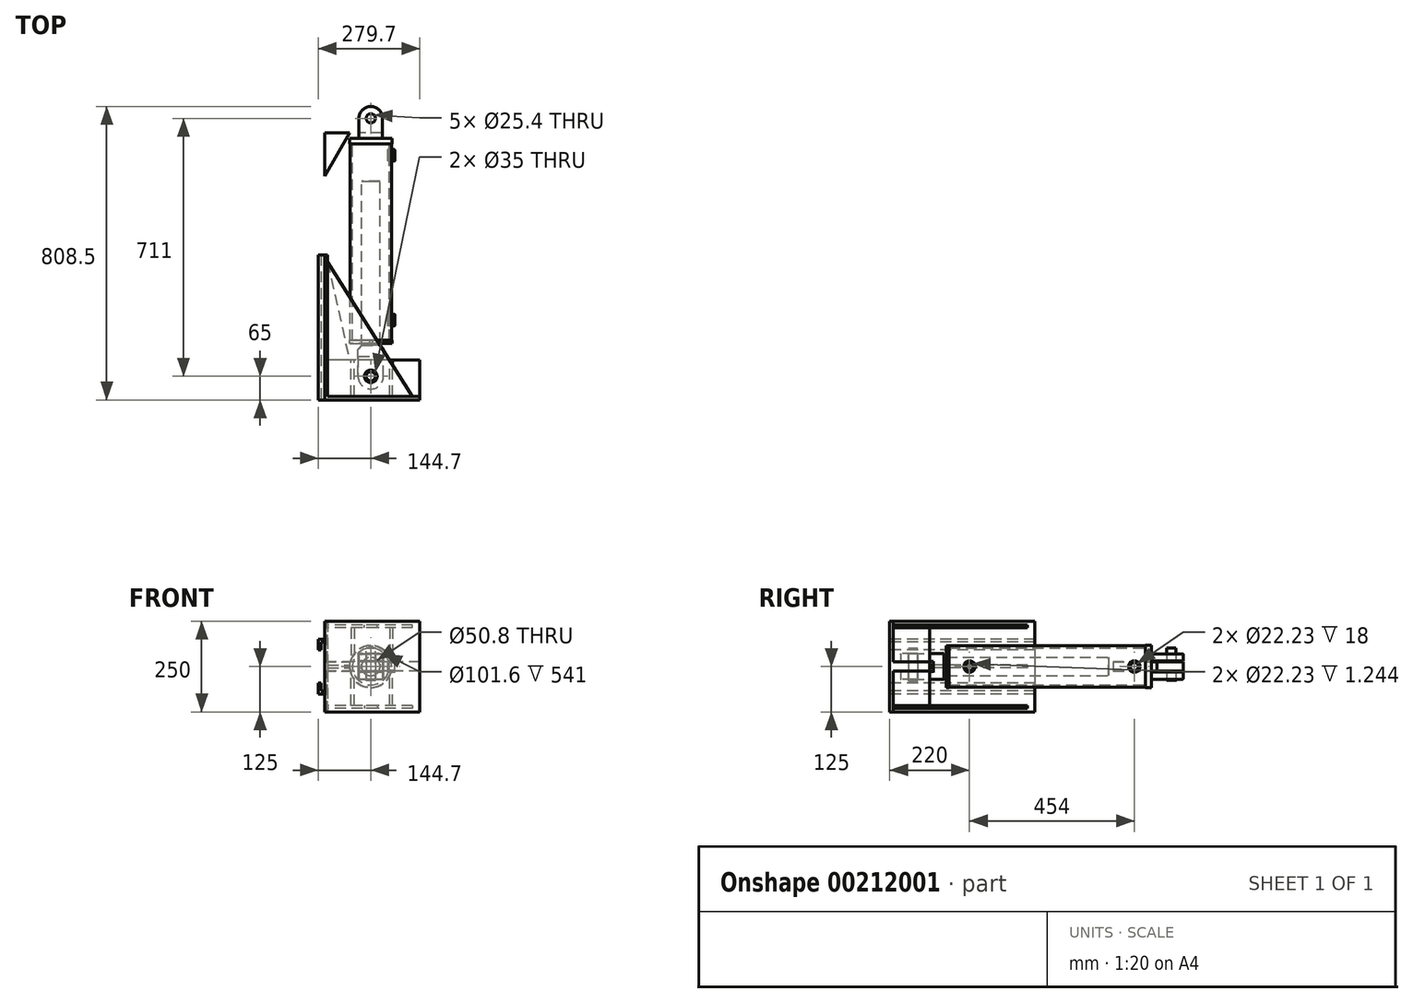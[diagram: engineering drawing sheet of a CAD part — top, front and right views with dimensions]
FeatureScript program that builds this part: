
annotation { "Feature Type Name" : "Feature", "Feature Type Description" : "" }
export const myFeature = defineFeature(function(context is Context, id is Id, definition is map)
    precondition{}
    {
        {
            assignVariable(context, id + "F0", {"name" : "Stroke", "anyValue" : 400});
        }
        {
            var Q0;
            Q0=qCreatedBy(makeId("Front.planeOp"),FACE);
            var sketch = newSketch(context, id + "F1", { "sketchPlane" : qUnion([Q0])});
            skCircle(sketch, "E0", {"center": v(0, 0) * mm, "radius": 50.8 * mm});
            skCircle(sketch, "E1", {"center": v(0, 0) * mm, "radius": 57.15 * mm});
            skSolve(sketch);
        }
        {
            var Q0;
            Q0=makeQuery(id+"F1.imprint","IMPRINT",FACE,{"disambiguationData":[TD([[makeQuery(id+"F1.imprint","IMPRINT",EDGE,{"derivedFrom":sQuery(id+"F1.wireOp",EDGE,"E0")}),-1.0]])]});
            extrude(context, id + "F2", {"entities" : qUnion([Q0]), "depth" : (getVariable(context, 'Stroke') + 141) * mm});
        }
        {
            var Q0;
            Q0=makeQuery(id+"F2.opExtrude","CAP_FACE",FACE,{"disambiguationData":[OSD([sQuery(id+"F1.wireOp",EDGE,"E0"),sQuery(id+"F1.wireOp",EDGE,"E1")])],"isStart":true});
            var sketch = newSketch(context, id + "F3", { "sketchPlane" : qUnion([Q0])});
            skCircle(sketch, "E2", {"center": v(0, 0) * mm, "radius": 58.15 * mm});
            skSolve(sketch);
        }
        {
            var Q0;
            Q0=makeQuery(id+"F3.imprint","IMPRINT",FACE,{"disambiguationData":[TD([[makeQuery(id+"F3.imprint","IMPRINT",EDGE,{"derivedFrom":makeQuery(id+"F2.opExtrude","CAP_EDGE",EDGE,{"disambiguationData":[OSD([sQuery(id+"F1.wireOp",EDGE,"E0")])],"isStart":true})}),1.0]])]});
            var Q1;
            Q1=makeQuery(id+"F3.imprint","IMPRINT",FACE,{"disambiguationData":[TD([[makeQuery(id+"F3.imprint","IMPRINT",EDGE,{"derivedFrom":sQuery(id+"F3.wireOp",EDGE,"E2")}),1.0]])]});
            var Q2;
            Q2=makeQuery(id+"F3.imprint","IMPRINT",FACE,{"disambiguationData":[TD([[makeQuery(id+"F3.imprint","IMPRINT",EDGE,{"derivedFrom":makeQuery(id+"F2.opExtrude","CAP_EDGE",EDGE,{"disambiguationData":[OSD([sQuery(id+"F1.wireOp",EDGE,"E0")])],"isStart":true})}),-1.0]])]});
            extrude(context, id + "F4", {"entities" : qUnion([Q0, Q1, Q2]), "depth" : 16 * mm});
        }
        {
            var Q0;
            Q0=makeQuery(id+"F2.opExtrude","CAP_FACE",FACE,{"disambiguationData":[OSD([sQuery(id+"F1.wireOp",EDGE,"E0"),sQuery(id+"F1.wireOp",EDGE,"E1")])],"isStart":false});
            var sketch = newSketch(context, id + "F5", { "sketchPlane" : qUnion([Q0])});
            skCircle(sketch, "E3", {"center": v(0, 0) * mm, "radius": 58.15 * mm});
            skCircle(sketch, "E4", {"center": v(0, 0) * mm, "radius": 25.4 * mm});
            skSolve(sketch);
        }
        {
            var Q0;
            Q0=makeQuery(id+"F5.imprint","IMPRINT",FACE,{"disambiguationData":[TD([[makeQuery(id+"F5.imprint","IMPRINT",EDGE,{"derivedFrom":makeQuery(id+"F2.opExtrude","CAP_EDGE",EDGE,{"disambiguationData":[OSD([sQuery(id+"F1.wireOp",EDGE,"E0")])],"isStart":false})}),-1.0]])]});
            var Q1;
            Q1=makeQuery(id+"F5.imprint","IMPRINT",FACE,{"disambiguationData":[TD([[makeQuery(id+"F5.imprint","IMPRINT",EDGE,{"derivedFrom":sQuery(id+"F5.wireOp",EDGE,"E4")}),-1.0]])]});
            var Q2;
            Q2=makeQuery(id+"F5.imprint","IMPRINT",FACE,{"disambiguationData":[TD([[makeQuery(id+"F5.imprint","IMPRINT",EDGE,{"derivedFrom":sQuery(id+"F5.wireOp",EDGE,"E3")}),1.0]])]});
            extrude(context, id + "F6", {"entities" : qUnion([Q0, Q1, Q2]), "depth" : 8 * mm});
        }
        {
            var Q0;
            Q0=makeQuery(id+"F6.opExtrude","CAP_FACE",FACE,{"disambiguationData":[OSD([sQuery(id+"F5.wireOp",EDGE,"E3"),sQuery(id+"F5.wireOp",EDGE,"E4")])],"isStart":false});
            var sketch = newSketch(context, id + "F7", { "sketchPlane" : qUnion([Q0])});
            skLineSegment(sketch, "E5", {"start": v(-3.5, 58.04) * mm, "end": v(-3.5, 54.04) * mm});
            skLineSegment(sketch, "E6", {"start": v(-3.5, 54.04) * mm, "end": v(3.5, 54.04) * mm});
            skLineSegment(sketch, "E7", {"start": v(3.5, 54.04) * mm, "end": v(3.5, 58.04) * mm});
            skPoint(sketch, "E8", {"position": v(0, 54.04) * mm});
            skCircle(sketch, "E9.0", {"center": v(0, 0) * mm, "radius": 58.15 * mm});
            skArc(sketch, "E10", {"start": v(-3.5, 58.04) * mm, "mid": v(0, 58.15) * mm, "end": v(3.5, 58.04) * mm});
            skSolve(sketch);
        }
        {
            var Q0;
            {var subQ0=sQuery(id+"F7.wireOp",EDGE,"E5");Q0=makeQuery(id+"F7.imprint","IMPRINT",FACE,{"disambiguationData":[TD([[makeQuery(id+"F7.imprint","IMPRINT",EDGE,{"derivedFrom":subQ0}),1.0]])]});}
            extrude(context, id + "F8", {"entities" : qUnion([Q0]), "operationType" : NewBodyOperationType.REMOVE, "endBound" : BoundingType.UP_TO_NEXT, "oppositeDirection" : true, "depth" : 25 * mm});
        }
        {
            var Q0;
            Q0=qCreatedBy(makeId("Top.planeOp"),FACE);
            var sketch = newSketch(context, id + "F9", { "sketchPlane" : qUnion([Q0])});
            skCircle(sketch, "E11", {"center": v(0, 71) * mm, "radius": 12.7 * mm});
            skCircle(sketch, "E12", {"center": v(0, 71) * mm, "radius": 32.5 * mm});
            skLineSegment(sketch, "E13.0", {"start": v(-58.15, 16) * mm, "end": v(58.15, 16) * mm});
            skLineSegment(sketch, "E14", {"start": v(-32.5, 16) * mm, "end": v(-32.5, 71) * mm});
            skLineSegment(sketch, "E15", {"start": v(32.5, 16) * mm, "end": v(32.5, 71) * mm});
            skSolve(sketch);
        }
        {
            var Q0;
            {var subQ0=sQuery(id+"F9.wireOp",EDGE,"E14");Q0=makeQuery(id+"F9.imprint","IMPRINT",FACE,{"disambiguationData":[TD([[makeQuery(id+"F9.imprint","IMPRINT",EDGE,{"derivedFrom":subQ0}),-1.0]])]});}
            var Q1;
            Q1=makeQuery(id+"F9.imprint","IMPRINT",FACE,{"disambiguationData":[TD([[makeQuery(id+"F9.imprint","IMPRINT",EDGE,{"derivedFrom":sQuery(id+"F9.wireOp",EDGE,"E11")}),-1.0]])]});
            extrude(context, id + "F10", {"entities" : qUnion([Q0, Q1]), "operationType" : NewBodyOperationType.ADD, "endBound" : BoundingType.SYMMETRIC, "depth" : 70 * mm});
        }
        {
            var Q0;
            {var subQ0=sQuery(id+"F9.wireOp",EDGE,"E14");Q0=makeQuery(id+"F9.imprint","IMPRINT",FACE,{"disambiguationData":[TD([[makeQuery(id+"F9.imprint","IMPRINT",EDGE,{"derivedFrom":subQ0}),-1.0]])]});}
            var Q1;
            Q1=makeQuery(id+"F9.imprint","IMPRINT",FACE,{"disambiguationData":[TD([[makeQuery(id+"F9.imprint","IMPRINT",EDGE,{"derivedFrom":sQuery(id+"F9.wireOp",EDGE,"E11")}),-1.0]])]});
            extrude(context, id + "F11", {"entities" : qUnion([Q0, Q1]), "operationType" : NewBodyOperationType.REMOVE, "endBound" : BoundingType.SYMMETRIC, "depth" : 30 * mm});
        }
        {
            var Q0;
            Q0=makeQuery(id+"F10.opExtrude","CAP_EDGE",EDGE,{"disambiguationData":[OSD([sQuery(id+"F9.wireOp",EDGE,"E13.0")])],"isStart":false});
            var Q1;
            {var subQ0=sQuery(id+"F9.wireOp",EDGE,"E14");var subQ1=sQuery(id+"F9.wireOp",EDGE,"E15");var subQ2=sQuery(id+"F9.wireOp",EDGE,"E13.0");var subQ3=sQuery(id+"F9.wireOp",EDGE,"E12");var subQ4=sQuery(id+"F9.wireOp",EDGE,"E11");Q1=makeQuery(id+"F11.boolean.opBoolean","SPLIT",EDGE,{"disambiguationData":[TD([makeQuery(id+"F10.opExtrude","CAP_FACE",FACE,{"disambiguationData":[OSD([subQ4,subQ3,subQ2,subQ0,subQ1])],"isStart":false})])],"derivedFrom":makeQuery(id+"F10.opExtrude","SWEPT_EDGE",EDGE,{"disambiguationData":[OSD([subQ2,subQ0])]})});}
            var Q2;
            Q2=makeQuery(id+"F11.boolean.opBoolean","COPY",EDGE,{"derivedFrom":makeQuery(id+"F11.opExtrude","CAP_EDGE",EDGE,{"disambiguationData":[OSD([sQuery(id+"F9.wireOp",EDGE,"E13.0")])],"isStart":false})});
            var Q3;
            Q3=makeQuery(id+"F10.opExtrude","CAP_EDGE",EDGE,{"disambiguationData":[OSD([sQuery(id+"F9.wireOp",EDGE,"E13.0")])],"isStart":true});
            var Q4;
            {var subQ0=sQuery(id+"F9.wireOp",EDGE,"E14");var subQ1=sQuery(id+"F9.wireOp",EDGE,"E15");var subQ2=sQuery(id+"F9.wireOp",EDGE,"E13.0");var subQ3=sQuery(id+"F9.wireOp",EDGE,"E12");var subQ4=sQuery(id+"F9.wireOp",EDGE,"E11");Q4=makeQuery(id+"F11.boolean.opBoolean","SPLIT",EDGE,{"disambiguationData":[TD([makeQuery(id+"F10.opExtrude","CAP_FACE",FACE,{"disambiguationData":[OSD([subQ4,subQ3,subQ2,subQ0,subQ1])],"isStart":true})])],"derivedFrom":makeQuery(id+"F10.opExtrude","SWEPT_EDGE",EDGE,{"disambiguationData":[OSD([subQ2,subQ0])]})});}
            var Q5;
            Q5=makeQuery(id+"F11.boolean.opBoolean","COPY",EDGE,{"derivedFrom":makeQuery(id+"F11.opExtrude","CAP_EDGE",EDGE,{"disambiguationData":[OSD([sQuery(id+"F9.wireOp",EDGE,"E13.0")])],"isStart":true})});
            var Q6;
            {var subQ0=sQuery(id+"F9.wireOp",EDGE,"E15");var subQ1=sQuery(id+"F9.wireOp",EDGE,"E14");var subQ2=sQuery(id+"F9.wireOp",EDGE,"E13.0");var subQ3=sQuery(id+"F9.wireOp",EDGE,"E12");var subQ4=sQuery(id+"F9.wireOp",EDGE,"E11");Q6=makeQuery(id+"F11.boolean.opBoolean","SPLIT",EDGE,{"disambiguationData":[TD([makeQuery(id+"F10.opExtrude","CAP_FACE",FACE,{"disambiguationData":[OSD([subQ4,subQ3,subQ2,subQ1,subQ0])],"isStart":true})])],"derivedFrom":makeQuery(id+"F10.opExtrude","SWEPT_EDGE",EDGE,{"disambiguationData":[OSD([subQ2,subQ0])]})});}
            var Q7;
            {var subQ0=sQuery(id+"F9.wireOp",EDGE,"E15");var subQ1=sQuery(id+"F9.wireOp",EDGE,"E14");var subQ2=sQuery(id+"F9.wireOp",EDGE,"E13.0");var subQ3=sQuery(id+"F9.wireOp",EDGE,"E12");var subQ4=sQuery(id+"F9.wireOp",EDGE,"E11");Q7=makeQuery(id+"F11.boolean.opBoolean","SPLIT",EDGE,{"disambiguationData":[TD([makeQuery(id+"F10.opExtrude","CAP_FACE",FACE,{"disambiguationData":[OSD([subQ4,subQ3,subQ2,subQ1,subQ0])],"isStart":false})])],"derivedFrom":makeQuery(id+"F10.opExtrude","SWEPT_EDGE",EDGE,{"disambiguationData":[OSD([subQ2,subQ0])]})});}
            fillet(context, id + "F12", {"entities" : qUnion([Q0, Q1, Q2, Q3, Q4, Q5, Q6, Q7]), "radius" : 3 * mm, "tangentPropagation" : true, "allowEdgeOverflow" : false});
        }
        {
            var Q0;
            Q0=makeQuery(id+"F11.boolean.opBoolean","COPY",EDGE,{"derivedFrom":makeQuery(id+"F11.opExtrude","CAP_EDGE",EDGE,{"disambiguationData":[OSD([sQuery(id+"F9.wireOp",EDGE,"E12")])],"isStart":true})});
            var Q1;
            Q1=makeQuery(id+"F11.boolean.opBoolean","COPY",EDGE,{"derivedFrom":makeQuery(id+"F11.opExtrude","CAP_EDGE",EDGE,{"disambiguationData":[OSD([sQuery(id+"F9.wireOp",EDGE,"E12")])],"isStart":false})});
            var Q2;
            Q2=makeQuery(id+"F10.opExtrude","CAP_EDGE",EDGE,{"disambiguationData":[OSD([sQuery(id+"F9.wireOp",EDGE,"E12")])],"isStart":false});
            var Q3;
            Q3=makeQuery(id+"F10.opExtrude","CAP_EDGE",EDGE,{"disambiguationData":[OSD([sQuery(id+"F9.wireOp",EDGE,"E12")])],"isStart":true});
            fillet(context, id + "F13", {"entities" : qUnion([Q0, Q1, Q2, Q3]), "radius" : 2 * mm, "tangentPropagation" : true, "allowEdgeOverflow" : false});
        }
        {
            var Q0;
            Q0=makeQuery(id+"F6.opExtrude","CAP_FACE",FACE,{"disambiguationData":[OSD([sQuery(id+"F5.wireOp",EDGE,"E3"),sQuery(id+"F5.wireOp",EDGE,"E4")])],"isStart":false});
            var sketch = newSketch(context, id + "F14", { "sketchPlane" : qUnion([Q0])});
            skCircle(sketch, "E16.0", {"center": v(0, 0) * mm, "radius": 25.4 * mm});
            skSolve(sketch);
        }
        {
            var Q0;
            Q0=makeQuery(id+"F14.imprint","IMPRINT",FACE,{"disambiguationData":[TD([[makeQuery(id+"F14.imprint","IMPRINT",EDGE,{"derivedFrom":sQuery(id+"F14.wireOp",EDGE,"E16.0")}),1.0]])]});
            extrude(context, id + "F15", {"entities" : qUnion([Q0]), "depth" : 6 * mm, "hasSecondDirection" : true, "secondDirectionOppositeDirection" : true, "secondDirectionDepth" : (getVariable(context, 'Stroke') + 47) * mm});
        }
        {
            var Q0;
            Q0=qCreatedBy(makeId("Top.planeOp"),FACE);
            var sketch = newSketch(context, id + "F16", { "sketchPlane" : qUnion([Q0])});
            skLineSegment(sketch, "E17.0", {"start": v(25.4, -555) * mm, "end": v(-25.4, -555) * mm});
            skCircle(sketch, "E18", {"center": v(0, -640) * mm, "radius": 12.7 * mm});
            skPoint(sketch, "E18.centerSnap0", {"position": v(0, -555) * mm});
            skCircle(sketch, "E19", {"center": v(0, -640) * mm, "radius": 35 * mm});
            skLineSegment(sketch, "E20", {"start": v(-35, -640) * mm, "end": v(-35, -555) * mm});
            skLineSegment(sketch, "E21", {"start": v(35, -640) * mm, "end": v(35, -555) * mm});
            skLineSegment(sketch, "E22", {"start": v(35, -555) * mm, "end": v(-35, -555) * mm});
            skLineSegment(sketch, "E23", {"start": v(-25.4, -555) * mm, "end": v(-35, -564.6) * mm});
            skLineSegment(sketch, "E24", {"start": v(25.4, -555) * mm, "end": v(35, -564.6) * mm});
            skSolve(sketch);
        }
        {
            var Q0;
            Q0=makeQuery(id+"F16.imprint","IMPRINT",FACE,{"disambiguationData":[TD([[makeQuery(id+"F16.imprint","IMPRINT",EDGE,{"derivedFrom":sQuery(id+"F16.wireOp",EDGE,"E18")}),-1.0]])]});
            var Q1;
            {var subQ0=sQuery(id+"F16.wireOp",EDGE,"E23");Q1=makeQuery(id+"F16.imprint","IMPRINT",FACE,{"disambiguationData":[TD([[makeQuery(id+"F16.imprint","IMPRINT",EDGE,{"derivedFrom":subQ0}),1.0]])]});}
            extrude(context, id + "F17", {"entities" : qUnion([Q0, Q1]), "operationType" : NewBodyOperationType.ADD, "endBound" : BoundingType.SYMMETRIC, "depth" : 71 * mm});
        }
        {
            var Q0;
            Q0=qCreatedBy(makeId("Top.planeOp"),FACE);
            var sketch = newSketch(context, id + "F18", { "sketchPlane" : qUnion([Q0])});
            skArc(sketch, "E25.0.0", {"start": v(-35, -640) * mm, "mid": v(0, -675) * mm, "end": v(35, -640) * mm});
            skLineSegment(sketch, "E25.0.1", {"start": v(35, -640) * mm, "end": v(35, -564.6) * mm});
            skLineSegment(sketch, "E25.0.2", {"start": v(35, -564.6) * mm, "end": v(25.4, -555) * mm});
            skLineSegment(sketch, "E25.0.3", {"start": v(25.4, -555) * mm, "end": v(-25.4, -555) * mm});
            skLineSegment(sketch, "E25.0.4", {"start": v(-25.4, -555) * mm, "end": v(-35, -564.6) * mm});
            skLineSegment(sketch, "E25.0.5", {"start": v(-35, -564.6) * mm, "end": v(-35, -640) * mm});
            skLineSegment(sketch, "E26", {"start": v(-35, -585) * mm, "end": v(35, -585) * mm});
            skSolve(sketch);
        }
        {
            var Q0;
            {var subQ0=sQuery(id+"F18.wireOp",EDGE,"E25.0.0");Q0=makeQuery(id+"F18.imprint","IMPRINT",FACE,{"disambiguationData":[TD([[makeQuery(id+"F18.imprint","IMPRINT",EDGE,{"derivedFrom":subQ0}),1.0]])]});}
            extrude(context, id + "F19", {"entities" : qUnion([Q0]), "operationType" : NewBodyOperationType.REMOVE, "endBound" : BoundingType.SYMMETRIC, "depth" : 28 * mm});
        }
        {
            var Q0;
            Q0=makeQuery(id+"F17.opExtrude","CAP_EDGE",EDGE,{"disambiguationData":[OSD([sQuery(id+"F16.wireOp",EDGE,"E20")])],"isStart":false});
            var Q1;
            Q1=makeQuery(id+"F17.opExtrude","CAP_EDGE",EDGE,{"disambiguationData":[OSD([sQuery(id+"F16.wireOp",EDGE,"E20")])],"isStart":true});
            var Q2;
            Q2=makeQuery(id+"F17.opExtrude","SWEPT_EDGE",EDGE,{"disambiguationData":[OSD([sQuery(id+"F16.wireOp",EDGE,"E20"),sQuery(id+"F16.wireOp",EDGE,"E23")])]});
            var Q3;
            Q3=makeQuery(id+"F17.opExtrude","CAP_EDGE",EDGE,{"disambiguationData":[OSD([sQuery(id+"F16.wireOp",EDGE,"E23")])],"isStart":false});
            var Q4;
            {var subQ0=sQuery(id+"F16.wireOp",EDGE,"E23");var subQ1=sQuery(id+"F16.wireOp",EDGE,"E22");Q4=makeQuery(id+"F17.boolean.opBoolean","SPLIT",EDGE,{"disambiguationData":[TD([makeQuery(id+"F17.opExtrude","CAP_FACE",FACE,{"disambiguationData":[OSD([sQuery(id+"F16.wireOp",EDGE,"E18"),sQuery(id+"F16.wireOp",EDGE,"E19"),sQuery(id+"F16.wireOp",EDGE,"E20"),sQuery(id+"F16.wireOp",EDGE,"E21"),subQ1,subQ0,sQuery(id+"F16.wireOp",EDGE,"E24")])],"isStart":false})])],"derivedFrom":makeQuery(id+"F17.opExtrude","SWEPT_EDGE",EDGE,{"disambiguationData":[OSD([subQ1,subQ0])]})});}
            var Q5;
            Q5=makeQuery(id+"F17.opExtrude","CAP_EDGE",EDGE,{"disambiguationData":[OSD([sQuery(id+"F16.wireOp",EDGE,"E23")])],"isStart":true});
            var Q6;
            Q6=makeQuery(id+"F17.opExtrude","CAP_EDGE",EDGE,{"disambiguationData":[OSD([sQuery(id+"F16.wireOp",EDGE,"E22")])],"isStart":false});
            var Q7;
            Q7=makeQuery(id+"F17.opExtrude","CAP_EDGE",EDGE,{"disambiguationData":[OSD([sQuery(id+"F16.wireOp",EDGE,"E24")])],"isStart":false});
            var Q8;
            Q8=makeQuery(id+"F17.opExtrude","SWEPT_EDGE",EDGE,{"disambiguationData":[OSD([sQuery(id+"F16.wireOp",EDGE,"E21"),sQuery(id+"F16.wireOp",EDGE,"E24")])]});
            var Q9;
            Q9=makeQuery(id+"F17.opExtrude","CAP_EDGE",EDGE,{"disambiguationData":[OSD([sQuery(id+"F16.wireOp",EDGE,"E24")])],"isStart":true});
            var Q10;
            {var subQ0=sQuery(id+"F16.wireOp",EDGE,"E24");var subQ1=sQuery(id+"F16.wireOp",EDGE,"E22");Q10=makeQuery(id+"F17.boolean.opBoolean","SPLIT",EDGE,{"disambiguationData":[TD([makeQuery(id+"F17.opExtrude","CAP_FACE",FACE,{"disambiguationData":[OSD([sQuery(id+"F16.wireOp",EDGE,"E18"),sQuery(id+"F16.wireOp",EDGE,"E19"),sQuery(id+"F16.wireOp",EDGE,"E20"),sQuery(id+"F16.wireOp",EDGE,"E21"),subQ1,sQuery(id+"F16.wireOp",EDGE,"E23"),subQ0])],"isStart":true})])],"derivedFrom":makeQuery(id+"F17.opExtrude","SWEPT_EDGE",EDGE,{"disambiguationData":[OSD([subQ1,subQ0])]})});}
            var Q11;
            {var subQ0=sQuery(id+"F16.wireOp",EDGE,"E24");var subQ1=sQuery(id+"F16.wireOp",EDGE,"E22");Q11=makeQuery(id+"F17.boolean.opBoolean","SPLIT",EDGE,{"disambiguationData":[TD([makeQuery(id+"F17.opExtrude","CAP_FACE",FACE,{"disambiguationData":[OSD([sQuery(id+"F16.wireOp",EDGE,"E18"),sQuery(id+"F16.wireOp",EDGE,"E19"),sQuery(id+"F16.wireOp",EDGE,"E20"),sQuery(id+"F16.wireOp",EDGE,"E21"),subQ1,sQuery(id+"F16.wireOp",EDGE,"E23"),subQ0])],"isStart":false})])],"derivedFrom":makeQuery(id+"F17.opExtrude","SWEPT_EDGE",EDGE,{"disambiguationData":[OSD([subQ1,subQ0])]})});}
            var Q12;
            Q12=makeQuery(id+"F17.opExtrude","CAP_EDGE",EDGE,{"disambiguationData":[OSD([sQuery(id+"F16.wireOp",EDGE,"E22")])],"isStart":true});
            var Q13;
            Q13=makeQuery(id+"F19.boolean.opBoolean","COPY",EDGE,{"derivedFrom":makeQuery(id+"F19.opExtrude","CAP_EDGE",EDGE,{"disambiguationData":[OSD([sQuery(id+"F18.wireOp",EDGE,"E25.0.5")])],"isStart":false})});
            var Q14;
            Q14=makeQuery(id+"F19.boolean.opBoolean","COPY",EDGE,{"derivedFrom":makeQuery(id+"F19.opExtrude","SWEPT_EDGE",EDGE,{"disambiguationData":[OSD([sQuery(id+"F18.wireOp",EDGE,"E25.0.5"),sQuery(id+"F18.wireOp",EDGE,"E26")])]})});
            var Q15;
            Q15=makeQuery(id+"F19.boolean.opBoolean","COPY",EDGE,{"derivedFrom":makeQuery(id+"F19.opExtrude","CAP_EDGE",EDGE,{"disambiguationData":[OSD([sQuery(id+"F18.wireOp",EDGE,"E25.0.0")])],"isStart":true})});
            var Q16;
            Q16=makeQuery(id+"F19.boolean.opBoolean","COPY",EDGE,{"derivedFrom":makeQuery(id+"F19.opExtrude","SWEPT_EDGE",EDGE,{"disambiguationData":[OSD([sQuery(id+"F18.wireOp",EDGE,"E25.0.1"),sQuery(id+"F18.wireOp",EDGE,"E26")])]})});
            fillet(context, id + "F20", {"entities" : qUnion([Q0, Q1, Q2, Q3, Q4, Q5, Q6, Q7, Q8, Q9, Q10, Q11, Q12, Q13, Q14, Q15, Q16]), "radius" : 2 * mm, "tangentPropagation" : true, "allowEdgeOverflow" : false});
        }
        {
            var Q0;
            Q0=qCreatedBy(makeId("Right.planeOp"),FACE);
            cPlane(context, id + "F21", {"entities" : qUnion([Q0]), "cplaneType" : CPlaneType.OFFSET, "offset" : 50.8 * mm + 1 / 101.6 * mm, "width" : 150 * mm, "height" : 150 * mm});
        }
        {
            var Q0;
            Q0=qCreatedBy(id+"F21.planeOp",FACE);
            var sketch = newSketch(context, id + "F22", { "sketchPlane" : qUnion([Q0])});
            skCircle(sketch, "E27", {"center": v(-31, 0) * mm, "radius": 15.88 * mm});
            skCircle(sketch, "E28", {"center": v(-485, 0) * mm, "radius": 15.88 * mm});
            skCircle(sketch, "E29", {"center": v(-485, 0) * mm, "radius": 11.11 * mm});
            skCircle(sketch, "E30", {"center": v(-31, 0) * mm, "radius": 11.11 * mm});
            skSolve(sketch);
        }
        {
            var Q0;
            Q0=makeQuery(id+"F22.imprint","IMPRINT",FACE,{"disambiguationData":[TD([[makeQuery(id+"F22.imprint","IMPRINT",EDGE,{"derivedFrom":sQuery(id+"F22.wireOp",EDGE,"E29")}),1.0]])]});
            var Q1;
            Q1=makeQuery(id+"F22.imprint","IMPRINT",FACE,{"disambiguationData":[TD([[makeQuery(id+"F22.imprint","IMPRINT",EDGE,{"derivedFrom":sQuery(id+"F22.wireOp",EDGE,"E30")}),1.0]])]});
            extrude(context, id + "F23", {"entities" : qUnion([Q0, Q1]), "operationType" : NewBodyOperationType.REMOVE, "endBound" : BoundingType.UP_TO_NEXT, "oppositeDirection" : true, "depth" : 25 * mm});
        }
        {
            var Q0;
            Q0=makeQuery(id+"F22.imprint","IMPRINT",FACE,{"disambiguationData":[TD([[makeQuery(id+"F22.imprint","IMPRINT",EDGE,{"derivedFrom":sQuery(id+"F22.wireOp",EDGE,"E28")}),1.0]])]});
            var Q1;
            Q1=makeQuery(id+"F22.imprint","IMPRINT",FACE,{"disambiguationData":[TD([[makeQuery(id+"F22.imprint","IMPRINT",EDGE,{"derivedFrom":sQuery(id+"F22.wireOp",EDGE,"E27")}),1.0]])]});
            extrude(context, id + "F24", {"entities" : qUnion([Q0, Q1]), "depth" : 15 * mm, "hasSecondDirection" : true, "secondDirectionOppositeDirection" : true, "secondDirectionDepth" : 4 * mm});
        }
        {
            var Q0;
            Q0=makeQuery(id+"F24.opExtrude","CAP_EDGE",EDGE,{"disambiguationData":[OSD([sQuery(id+"F22.wireOp",EDGE,"E28")])],"isStart":false});
            var Q1;
            Q1=makeQuery(id+"F24.opExtrude","CAP_EDGE",EDGE,{"disambiguationData":[OSD([sQuery(id+"F22.wireOp",EDGE,"E29")])],"isStart":false});
            var Q2;
            Q2=makeQuery(id+"F24.opExtrude","CAP_EDGE",EDGE,{"disambiguationData":[OSD([sQuery(id+"F22.wireOp",EDGE,"E30")])],"isStart":false});
            var Q3;
            Q3=makeQuery(id+"F24.opExtrude","CAP_EDGE",EDGE,{"disambiguationData":[OSD([sQuery(id+"F22.wireOp",EDGE,"E27")])],"isStart":false});
            fillet(context, id + "F25", {"entities" : qUnion([Q0, Q1, Q2, Q3]), "radius" : 1 * mm, "tangentPropagation" : true, "allowEdgeOverflow" : false});
        }
        {
            var Q0;
            Q0=makeQuery(id+"F17.opExtrude","CAP_FACE",FACE,{"disambiguationData":[OSD([sQuery(id+"F16.wireOp",EDGE,"E18"),sQuery(id+"F16.wireOp",EDGE,"E19"),sQuery(id+"F16.wireOp",EDGE,"E20"),sQuery(id+"F16.wireOp",EDGE,"E21"),sQuery(id+"F16.wireOp",EDGE,"E22"),sQuery(id+"F16.wireOp",EDGE,"E23"),sQuery(id+"F16.wireOp",EDGE,"E24")])],"isStart":true});
            var sketch = newSketch(context, id + "F26", { "sketchPlane" : qUnion([Q0])});
            skCircle(sketch, "E31.0", {"center": v(0, 640) * mm, "radius": 12.7 * mm});
            skSolve(sketch);
        }
        {
            var Q0;
            Q0=makeQuery(id+"F26.imprint","IMPRINT",FACE,{"disambiguationData":[TD([[makeQuery(id+"F26.imprint","IMPRINT",EDGE,{"derivedFrom":sQuery(id+"F26.wireOp",EDGE,"E31.0")}),-1.0]])]});
            extrude(context, id + "F27", {"entities" : qUnion([Q0]), "depth" : 3 * mm, "hasSecondDirection" : true, "secondDirectionOppositeDirection" : true, "secondDirectionDepth" : 85 * mm});
        }
        {
            var Q0;
            Q0=makeQuery(id+"F10.opExtrude","CAP_FACE",FACE,{"disambiguationData":[OSD([sQuery(id+"F9.wireOp",EDGE,"E11"),sQuery(id+"F9.wireOp",EDGE,"E12"),sQuery(id+"F9.wireOp",EDGE,"E13.0"),sQuery(id+"F9.wireOp",EDGE,"E14"),sQuery(id+"F9.wireOp",EDGE,"E15")])],"isStart":true});
            var sketch = newSketch(context, id + "F28", { "sketchPlane" : qUnion([Q0])});
            skCircle(sketch, "E32.0", {"center": v(0, -71) * mm, "radius": 12.7 * mm});
            skSolve(sketch);
        }
        {
            var Q0;
            Q0=makeQuery(id+"F28.imprint","IMPRINT",FACE,{"disambiguationData":[TD([[makeQuery(id+"F28.imprint","IMPRINT",EDGE,{"derivedFrom":sQuery(id+"F28.wireOp",EDGE,"E32.0")}),-1.0]])]});
            extrude(context, id + "F29", {"entities" : qUnion([Q0]), "depth" : 3 * mm, "hasSecondDirection" : true, "secondDirectionOppositeDirection" : true, "secondDirectionDepth" : 86 * mm});
        }
        {
            var Q0;
            Q0=qCreatedBy(makeId("Top.planeOp"),FACE);
            var sketch = newSketch(context, id + "F30", { "sketchPlane" : qUnion([Q0])});
            skCircle(sketch, "E33.0", {"center": v(0, 71) * mm, "radius": 12.7 * mm});
            skLineSegment(sketch, "E34.0.0", {"start": v(-30.5, 19) * mm, "end": v(30.5, 19) * mm});
            skLineSegment(sketch, "E34.0.1", {"start": v(30.5, 19) * mm, "end": v(30.5, 71) * mm});
            skArc(sketch, "E34.0.2", {"start": v(30.5, 71) * mm, "mid": v(0, 101.5) * mm, "end": v(-30.5, 71) * mm});
            skLineSegment(sketch, "E34.0.3", {"start": v(-30.5, 71) * mm, "end": v(-30.5, 19) * mm});
            skLineSegment(sketch, "E35.0", {"start": v(32.5, 71) * mm, "end": v(32.5, 19) * mm});
            skArc(sketch, "E36.0", {"start": v(-32.5, 71) * mm, "mid": v(0, 103.5) * mm, "end": v(32.5, 71) * mm});
            skLineSegment(sketch, "E37.0", {"start": v(-32.5, 19) * mm, "end": v(-32.5, 71) * mm});
            skLineSegment(sketch, "E38.bottom", {"start": v(33, 131) * mm, "end": v(-127, 131) * mm});
            skLineSegment(sketch, "E38.top", {"start": v(33, 31) * mm, "end": v(-127, 31) * mm});
            skLineSegment(sketch, "E38.left", {"start": v(33, 131) * mm, "end": v(33, 31) * mm});
            skLineSegment(sketch, "E38.right", {"start": v(-127, 131) * mm, "end": v(-127, 31) * mm});
            skLineSegment(sketch, "E39", {"start": v(-127, 31) * mm, "end": v(-127, -89) * mm});
            skLineSegment(sketch, "E40", {"start": v(-127, -89) * mm, "end": v(-57.72, 31) * mm});
            skSolve(sketch);
        }
        {
            var Q0;
            {var subQ1=sQuery(id+"F30.wireOp",EDGE,"E36.0");Q0=makeQuery(id+"F30.imprint","IMPRINT",FACE,{"disambiguationData":[TD([[makeQuery(id+"F30.imprint","IMPRINT",EDGE,{"derivedFrom":subQ1}),1.0]])]});}
            var Q1;
            Q1=makeQuery(id+"F30.imprint","IMPRINT",FACE,{"disambiguationData":[TD([[makeQuery(id+"F30.imprint","IMPRINT",EDGE,{"derivedFrom":sQuery(id+"F30.wireOp",EDGE,"E33.0")}),-1.0]])]});
            var Q2;
            {var subQ0=sQuery(id+"F30.wireOp",EDGE,"E39");Q2=makeQuery(id+"F30.imprint","IMPRINT",FACE,{"disambiguationData":[TD([[makeQuery(id+"F30.imprint","IMPRINT",EDGE,{"derivedFrom":subQ0}),1.0]])]});}
            var Q3;
            {var subQ5=sQuery(id+"F30.wireOp",EDGE,"E34.0.2");Q3=makeQuery(id+"F30.imprint","IMPRINT",FACE,{"disambiguationData":[TD([[makeQuery(id+"F30.imprint","IMPRINT",EDGE,{"derivedFrom":subQ5}),-1.0]])]});}
            extrude(context, id + "F31", {"entities" : qUnion([Q0, Q1, Q2, Q3]), "operationType" : NewBodyOperationType.ADD, "endBound" : BoundingType.SYMMETRIC, "depth" : 25 * mm});
        }
        {
            var Q0;
            Q0=qCreatedBy(makeId("Top.planeOp"),FACE);
            var sketch = newSketch(context, id + "F32", { "sketchPlane" : qUnion([Q0])});
            skCircle(sketch, "E41.0", {"center": v(0, -640) * mm, "radius": 12.7 * mm});
            skLineSegment(sketch, "E42.0.0", {"start": v(33, -585) * mm, "end": v(-33, -585) * mm});
            skLineSegment(sketch, "E42.0.1", {"start": v(-33, -585) * mm, "end": v(-33, -640) * mm});
            skArc(sketch, "E42.0.2", {"start": v(-33, -640) * mm, "mid": v(0, -673) * mm, "end": v(33, -640) * mm});
            skLineSegment(sketch, "E42.0.3", {"start": v(33, -640) * mm, "end": v(33, -585) * mm});
            skLineSegment(sketch, "E43.bottom", {"start": v(135, -595) * mm, "end": v(-119, -595) * mm});
            skLineSegment(sketch, "E43.top", {"start": v(135, -695) * mm, "end": v(-119, -695) * mm});
            skLineSegment(sketch, "E43.left", {"start": v(135, -595) * mm, "end": v(135, -695) * mm});
            skLineSegment(sketch, "E43.right", {"start": v(-119, -595) * mm, "end": v(-119, -695) * mm});
            skSolve(sketch);
        }
        {
            var Q0;
            {var subQ4=sQuery(id+"F32.wireOp",EDGE,"E42.0.2");Q0=makeQuery(id+"F32.imprint","IMPRINT",FACE,{"disambiguationData":[TD([[makeQuery(id+"F32.imprint","IMPRINT",EDGE,{"derivedFrom":subQ4}),-1.0]])]});}
            var Q1;
            Q1=makeQuery(id+"F32.imprint","IMPRINT",FACE,{"disambiguationData":[TD([[makeQuery(id+"F32.imprint","IMPRINT",EDGE,{"derivedFrom":sQuery(id+"F32.wireOp",EDGE,"E41.0")}),-1.0]])]});
            extrude(context, id + "F33", {"entities" : qUnion([Q0, Q1]), "endBound" : BoundingType.SYMMETRIC, "depth" : 25 * mm});
        }
        {
            var Q0;
            Q0=makeQuery(id+"F33.opExtrude","SWEPT_FACE",FACE,{"disambiguationData":[OSD([sQuery(id+"F32.wireOp",EDGE,"E43.left")])]});
            var sketch = newSketch(context, id + "F34", { "sketchPlane" : qUnion([Q0])});
            skLineSegment(sketch, "E44.0.0", {"start": v(-695, -12.5) * mm, "end": v(-595, -12.5) * mm});
            skLineSegment(sketch, "E44.0.1", {"start": v(-595, -12.5) * mm, "end": v(-595, 12.5) * mm});
            skLineSegment(sketch, "E44.0.2", {"start": v(-595, 12.5) * mm, "end": v(-695, 12.5) * mm});
            skLineSegment(sketch, "E44.0.3", {"start": v(-695, 12.5) * mm, "end": v(-695, -12.5) * mm});
            skLineSegment(sketch, "E45.bottom", {"start": v(-695, -125) * mm, "end": v(-705, -125) * mm});
            skLineSegment(sketch, "E45.top", {"start": v(-695, 125) * mm, "end": v(-705, 125) * mm});
            skLineSegment(sketch, "E45.left", {"start": v(-695, -125) * mm, "end": v(-695, 125) * mm});
            skLineSegment(sketch, "E45.right", {"start": v(-705, -125) * mm, "end": v(-705, 125) * mm});
            skPoint(sketch, "E46", {"position": v(-695, 0) * mm});
            skSolve(sketch);
        }
        {
            var Q0;
            {var subQ3=sQuery(id+"F34.wireOp",EDGE,"E45.bottom");Q0=makeQuery(id+"F34.imprint","IMPRINT",FACE,{"disambiguationData":[TD([[makeQuery(id+"F34.imprint","IMPRINT",EDGE,{"derivedFrom":subQ3}),-1.0]])]});}
            var Q1;
            Q1=makeQuery(id+"F33.opExtrude","SWEPT_FACE",FACE,{"disambiguationData":[OSD([sQuery(id+"F32.wireOp",EDGE,"E43.right")])]});
            extrude(context, id + "F35", {"entities" : qUnion([Q0]), "operationType" : NewBodyOperationType.ADD, "endBound" : BoundingType.UP_TO_SURFACE, "oppositeDirection" : true, "endBoundEntityFace" : qUnion([Q1]), "depth" : 25 * mm});
        }
        {
            var Q0;
            Q0=makeQuery(id+"F35.opExtrude","SWEPT_FACE",FACE,{"disambiguationData":[OSD([sQuery(id+"F34.wireOp",EDGE,"E45.right")])]});
            var sketch = newSketch(context, id + "F36", { "sketchPlane" : qUnion([Q0])});
            skLineSegment(sketch, "E47.0", {"start": v(-119, 125) * mm, "end": v(-119, -125) * mm});
            skLineSegment(sketch, "E48", {"start": v(-119, 125) * mm, "end": v(-127, 125) * mm});
            skLineSegment(sketch, "E49", {"start": v(-127, 125) * mm, "end": v(-127, -125) * mm});
            skLineSegment(sketch, "E50", {"start": v(-127, -125) * mm, "end": v(-119, -125) * mm});
            skSolve(sketch);
        }
        {
            var Q0;
            Q0=makeQuery(id+"F36.imprint","IMPRINT",FACE,{"disambiguationData":[TD([[makeQuery(id+"F36.imprint","IMPRINT",EDGE,{"derivedFrom":sQuery(id+"F36.wireOp",EDGE,"E47.0")}),-1.0]])]});
            extrude(context, id + "F37", {"entities" : qUnion([Q0]), "operationType" : NewBodyOperationType.ADD, "oppositeDirection" : true, "depth" : 400 * mm});
        }
        {
            var Q0;
            Q0=qCreatedBy(makeId("Top.planeOp"),FACE);
            var sketch = newSketch(context, id + "F38", { "sketchPlane" : qUnion([Q0])});
            skLineSegment(sketch, "E51.0", {"start": v(-119, -305) * mm, "end": v(-119, -695) * mm});
            skLineSegment(sketch, "E52.0", {"start": v(135, -595) * mm, "end": v(-119, -595) * mm});
            skLineSegment(sketch, "E53", {"start": v(-119, -325) * mm, "end": v(-59, -595) * mm});
            skSolve(sketch);
        }
        {
            var Q0;
            {var subQ3=sQuery(id+"F38.wireOp",EDGE,"E53");Q0=makeQuery(id+"F38.imprint","IMPRINT",FACE,{"disambiguationData":[TD([[makeQuery(id+"F38.imprint","IMPRINT",EDGE,{"derivedFrom":subQ3}),-1.0]])]});}
            extrude(context, id + "F39", {"entities" : qUnion([Q0]), "endBound" : BoundingType.SYMMETRIC, "depth" : 8 * mm});
        }
        {
            var Q0;
            Q0=makeQuery(id+"F37.boolean.opBoolean","MERGE",FACE,{"derivedFrom":[makeQuery(id+"F35.opExtrude","SWEPT_FACE",FACE,{"disambiguationData":[OSD([sQuery(id+"F34.wireOp",EDGE,"E45.top")])]}),makeQuery(id+"F37.opExtrude","SWEPT_FACE",FACE,{"disambiguationData":[OSD([sQuery(id+"F36.wireOp",EDGE,"E48")])]})]});
            cPlane(context, id + "F40", {"entities" : qUnion([Q0]), "cplaneType" : CPlaneType.OFFSET, "offset" : 10 * mm, "oppositeDirection" : true, "width" : 150 * mm, "height" : 150 * mm});
        }
        {
            var Q0;
            Q0=qCreatedBy(id+"F40.planeOp",FACE);
            var sketch = newSketch(context, id + "F41", { "sketchPlane" : qUnion([Q0])});
            skCircle(sketch, "E54.0", {"center": v(0, -640) * mm, "radius": 12.7 * mm});
            skLineSegment(sketch, "E55.0", {"start": v(-119, -695) * mm, "end": v(135, -695) * mm});
            skLineSegment(sketch, "E56.0", {"start": v(-119, -305) * mm, "end": v(-119, -695) * mm});
            skLineSegment(sketch, "E57.0", {"start": v(-119, -325) * mm, "end": v(-59, -595) * mm});
            skLineSegment(sketch, "E58", {"start": v(115, -695) * mm, "end": v(-119, -325) * mm});
            skCircle(sketch, "E59", {"center": v(0, -640) * mm, "radius": 17.5 * mm});
            skSolve(sketch);
        }
        {
            var Q0;
            {var subQ0=sQuery(id+"F41.wireOp",EDGE,"E58");Q0=makeQuery(id+"F41.imprint","IMPRINT",FACE,{"disambiguationData":[TD([[makeQuery(id+"F41.imprint","IMPRINT",EDGE,{"derivedFrom":subQ0}),1.0]])]});}
            extrude(context, id + "F42", {"entities" : qUnion([Q0]), "oppositeDirection" : true, "depth" : 8 * mm});
        }
        {
            var Q0;
            Q0=makeQuery(id+"F42.opExtrude","SWEPT_BODY",BODY,{"disambiguationData":[OSD([sQuery(id+"F41.wireOp",EDGE,"E55.0"),sQuery(id+"F41.wireOp",EDGE,"E56.0"),sQuery(id+"F41.wireOp",EDGE,"E58"),sQuery(id+"F41.wireOp",EDGE,"E59"),sQuery(id+"F41.wireOp",EDGE,"cBHA6NDZ-MiiE-JSDo-Pbnv-cJdxclkFjxML")])]});
            var Q1;
            Q1=qCreatedBy(makeId("Top.planeOp"),FACE);
            mirror(context, id + "F43", {"entities" : qUnion([Q0]), "mirrorPlane" : qUnion([Q1])});
        }
        {
            var Q0;
            Q0=makeQuery(id+"F37.boolean.opBoolean","MERGE",FACE,{"derivedFrom":[makeQuery(id+"F35.opExtrude","SWEPT_FACE",FACE,{"disambiguationData":[OSD([sQuery(id+"F34.wireOp",EDGE,"E45.right")])]}),makeQuery(id+"F37.opExtrude","CAP_FACE",FACE,{"disambiguationData":[OSD([sQuery(id+"F36.wireOp",EDGE,"E47.0"),sQuery(id+"F36.wireOp",EDGE,"E48"),sQuery(id+"F36.wireOp",EDGE,"E49"),sQuery(id+"F36.wireOp",EDGE,"E50")])],"isStart":true})]});
            var sketch = newSketch(context, id + "F44", { "sketchPlane" : qUnion([Q0])});
            skLineSegment(sketch, "E60.0", {"start": v(-127, 125) * mm, "end": v(-127, -125) * mm});
            skPoint(sketch, "E61", {"position": v(-127, 0) * mm});
            skLineSegment(sketch, "E62", {"start": v(-127, 67.5) * mm, "end": v(-136.7, 67.5) * mm});
            skLineSegment(sketch, "E63", {"start": v(-136.7, 67.5) * mm, "end": v(-136.7, 45.5) * mm});
            skLineSegment(sketch, "E64", {"start": v(-136.7, 45.5) * mm, "end": v(-144.7, 45.5) * mm});
            skLineSegment(sketch, "E65", {"start": v(-144.7, 45.5) * mm, "end": v(-144.7, 75.5) * mm});
            skLineSegment(sketch, "E66", {"start": v(-144.7, 75.5) * mm, "end": v(-127, 75.5) * mm});
            skSolve(sketch);
        }
        {
            var Q0;
            {var subQ0=sQuery(id+"F44.wireOp",EDGE,"E62");Q0=makeQuery(id+"F44.imprint","IMPRINT",FACE,{"disambiguationData":[TD([[makeQuery(id+"F44.imprint","IMPRINT",EDGE,{"derivedFrom":subQ0}),-1.0]])]});}
            var Q1;
            Q1=makeQuery(id+"F37.opExtrude","CAP_FACE",FACE,{"disambiguationData":[OSD([sQuery(id+"F36.wireOp",EDGE,"E47.0"),sQuery(id+"F36.wireOp",EDGE,"E48"),sQuery(id+"F36.wireOp",EDGE,"E49"),sQuery(id+"F36.wireOp",EDGE,"E50")])],"isStart":false});
            extrude(context, id + "F45", {"entities" : qUnion([Q0]), "endBound" : BoundingType.UP_TO_SURFACE, "oppositeDirection" : true, "endBoundEntityFace" : qUnion([Q1]), "depth" : 25 * mm});
        }
        {
            var Q0;
            Q0=makeQuery(id+"F45.opExtrude","SWEPT_BODY",BODY,{"disambiguationData":[OSD([sQuery(id+"F44.wireOp",EDGE,"E60.0"),sQuery(id+"F44.wireOp",EDGE,"E62"),sQuery(id+"F44.wireOp",EDGE,"E63"),sQuery(id+"F44.wireOp",EDGE,"E64"),sQuery(id+"F44.wireOp",EDGE,"E65"),sQuery(id+"F44.wireOp",EDGE,"E66")])]});
            var Q1;
            Q1=qCreatedBy(makeId("Top.planeOp"),FACE);
            mirror(context, id + "F46", {"entities" : qUnion([Q0]), "mirrorPlane" : qUnion([Q1])});
        }
        {
            var Q0;
            Q0=makeQuery(id+"F33.opExtrude","CAP_FACE",FACE,{"disambiguationData":[OSD([sQuery(id+"F32.wireOp",EDGE,"E41.0"),sQuery(id+"F32.wireOp",EDGE,"E43.bottom"),sQuery(id+"F32.wireOp",EDGE,"E43.top"),sQuery(id+"F32.wireOp",EDGE,"E43.left"),sQuery(id+"F32.wireOp",EDGE,"E43.right")])],"isStart":true});
            var sketch = newSketch(context, id + "F47", { "sketchPlane" : qUnion([Q0])});
            skLineSegment(sketch, "E67.bottom", {"start": v(-46, 695) * mm, "end": v(-54, 695) * mm});
            skLineSegment(sketch, "E67.top", {"start": v(-46, 595) * mm, "end": v(-54, 595) * mm});
            skLineSegment(sketch, "E67.left", {"start": v(-46, 695) * mm, "end": v(-46, 595) * mm});
            skLineSegment(sketch, "E67.right", {"start": v(-54, 695) * mm, "end": v(-54, 595) * mm});
            skLineSegment(sketch, "E68.bottom", {"start": v(60, 695) * mm, "end": v(52, 695) * mm});
            skLineSegment(sketch, "E68.top", {"start": v(60, 595) * mm, "end": v(52, 595) * mm});
            skLineSegment(sketch, "E68.left", {"start": v(60, 695) * mm, "end": v(60, 595) * mm});
            skLineSegment(sketch, "E68.right", {"start": v(52, 695) * mm, "end": v(52, 595) * mm});
            skSolve(sketch);
        }
        {
            var Q0;
            Q0=makeQuery(id+"F47.imprint","IMPRINT",FACE,{"disambiguationData":[TD([[makeQuery(id+"F47.imprint","IMPRINT",EDGE,{"derivedFrom":sQuery(id+"F47.wireOp",EDGE,"E68.bottom")}),1.0]])]});
            var Q1;
            Q1=makeQuery(id+"F47.imprint","IMPRINT",FACE,{"disambiguationData":[TD([[makeQuery(id+"F47.imprint","IMPRINT",EDGE,{"derivedFrom":sQuery(id+"F47.wireOp",EDGE,"E67.bottom")}),1.0]])]});
            var Q2;
            Q2=makeQuery(id+"F43.opPattern","COPY",FACE,{"derivedFrom":makeQuery(id+"F42.opExtrude","CAP_FACE",FACE,{"disambiguationData":[OSD([sQuery(id+"F41.wireOp",EDGE,"E55.0"),sQuery(id+"F41.wireOp",EDGE,"E56.0"),sQuery(id+"F41.wireOp",EDGE,"E58"),sQuery(id+"F41.wireOp",EDGE,"E59")])],"isStart":false}),"instanceName":"1"});
            extrude(context, id + "F48", {"entities" : qUnion([Q0, Q1]), "endBound" : BoundingType.UP_TO_SURFACE, "endBoundEntityFace" : qUnion([Q2]), "depth" : 25 * mm});
        }
        {
            var Q0;
            Q0=makeQuery(id+"F48.opExtrude","SWEPT_BODY",BODY,{"disambiguationData":[OSD([sQuery(id+"F47.wireOp",EDGE,"E68.bottom"),sQuery(id+"F47.wireOp",EDGE,"E68.top"),sQuery(id+"F47.wireOp",EDGE,"E68.left"),sQuery(id+"F47.wireOp",EDGE,"E68.right")])]});
            var Q1;
            Q1=makeQuery(id+"F48.opExtrude","SWEPT_BODY",BODY,{"disambiguationData":[OSD([sQuery(id+"F47.wireOp",EDGE,"E67.bottom"),sQuery(id+"F47.wireOp",EDGE,"E67.top"),sQuery(id+"F47.wireOp",EDGE,"E67.left"),sQuery(id+"F47.wireOp",EDGE,"E67.right")])]});
            var Q2;
            Q2=qCreatedBy(makeId("Top.planeOp"),FACE);
            mirror(context, id + "F49", {"entities" : qUnion([Q0, Q1]), "mirrorPlane" : qUnion([Q2])});
        }
    });
